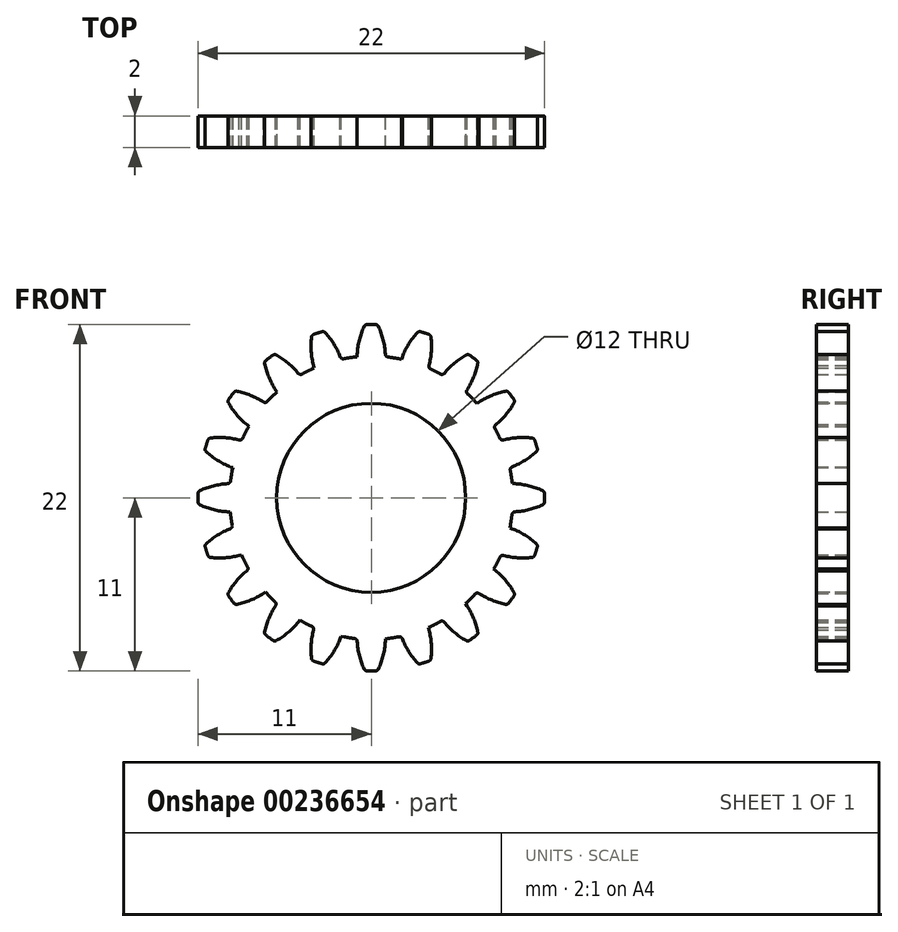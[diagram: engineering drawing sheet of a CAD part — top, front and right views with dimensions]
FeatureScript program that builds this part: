
annotation { "Feature Type Name" : "Feature", "Feature Type Description" : "" }
export const myFeature = defineFeature(function(context is Context, id is Id, definition is map)
    precondition{}
    {
        {
            var Q0;
            Q0=qCreatedBy(makeId("Front.planeOp"),FACE);
            var sketch = newSketch(context, id + "F0", { "sketchPlane" : qUnion([Q0])});
            skArc(sketch, "E0.0", {"start": v(1.74, 8.83) * mm, "mid": v(1.4, 8.89) * mm, "end": v(1.07, 8.94) * mm});
            skArc(sketch, "E1", {"start": v(0.9, 9.12) * mm, "mid": v(0.76, 10.02) * mm, "end": v(0.45, 10.88) * mm});
            skArc(sketch, "E2.MirrorCS", {"start": v(-0.9, 9.12) * mm, "mid": v(-0.76, 10.02) * mm, "end": v(-0.45, 10.88) * mm});
            skArc(sketch, "E3.trimOffspring", {"start": v(0.28, 11) * mm, "mid": v(0, 11) * mm, "end": v(-0.28, 11) * mm});
            skPoint(sketch, "E4.visualSharp", {"position": v(0.9, 8.95) * mm});
            skArc(sketch, "E4.filletArc", {"start": v(0.9, 9.12) * mm, "mid": v(0.95, 9) * mm, "end": v(1.07, 8.94) * mm});
            skPoint(sketch, "E5.visualSharp", {"position": v(-0.9, 8.95) * mm});
            skPoint(sketch, "E6.visualSharp", {"position": v(10.33, 3.78) * mm});
            skPoint(sketch, "E7.visualSharp", {"position": v(1.91, 8.8) * mm});
            skPoint(sketch, "E8.visualSharp", {"position": v(-0.4, 11) * mm});
            skArc(sketch, "E8.filletArc", {"start": v(-0.28, 11) * mm, "mid": v(-0.38, 10.96) * mm, "end": v(-0.45, 10.88) * mm});
            skPoint(sketch, "E9.visualSharp", {"position": v(0.4, 11) * mm});
            skArc(sketch, "E9.filletArc", {"start": v(0.45, 10.88) * mm, "mid": v(0.38, 10.96) * mm, "end": v(0.28, 11) * mm});
            skPoint(sketch, "E10.orphan", {"position": v(6.72, 6) * mm});
            skPoint(sketch, "E11.orphan", {"position": v(8.24, -3.62) * mm});
            skPoint(sketch, "E12.orphan", {"position": v(3.02, -10.58) * mm});
            skPoint(sketch, "E13.orphan", {"position": v(-6.78, -8.66) * mm});
            skPoint(sketch, "E14.orphan", {"position": v(-8.66, -6.78) * mm});
            skPoint(sketch, "E15.orphan", {"position": v(-9.13, -6.14) * mm});
            skPoint(sketch, "E16.orphan", {"position": v(-10.58, -3.02) * mm});
            skPoint(sketch, "E17.orphan", {"position": v(-11, 0.4) * mm});
            skPoint(sketch, "E18.orphan", {"position": v(-8.8, 1.91) * mm});
            skPoint(sketch, "E19.orphan", {"position": v(-10.33, 3.78) * mm});
            skPoint(sketch, "E20.orphan", {"position": v(-8.66, 6.78) * mm});
            skPoint(sketch, "E21.orphan", {"position": v(-4.54, 7.77) * mm});
            skLineSegment(sketch, "E22", {"start": v(0, 0) * mm, "end": v(-0.9, 8.95) * mm});
            skLineSegment(sketch, "E23", {"start": v(-0.9, 9.12) * mm, "end": v(-0.9, 8.95) * mm});
            skLineSegment(sketch, "E24", {"start": v(1.74, 8.83) * mm, "end": v(1.91, 8.8) * mm});
            skLineSegment(sketch, "E25", {"start": v(1.91, 8.8) * mm, "end": v(0, 0) * mm});
            skSolve(sketch);
        }
        {
            var Q0;
            Q0=makeQuery(id+"F0.imprint","IMPRINT",FACE,{"disambiguationData":[TD([[makeQuery(id+"F0.imprint","IMPRINT",EDGE,{"derivedFrom":sQuery(id+"F0.wireOp",EDGE,"E0.0")}),1.0]])]});
            extrude(context, id + "F1", {"entities" : qUnion([Q0]), "depth" : 2 * mm});
        }
        {
            var Q0;
            Q0=makeQuery(id+"F1.opExtrude","SWEPT_BODY",BODY,{"disambiguationData":[OSD([sQuery(id+"F0.wireOp",EDGE,"E0.0"),sQuery(id+"F0.wireOp",EDGE,"E1"),sQuery(id+"F0.wireOp",EDGE,"E2.MirrorCS"),sQuery(id+"F0.wireOp",EDGE,"E3.trimOffspring"),sQuery(id+"F0.wireOp",EDGE,"E4.filletArc"),sQuery(id+"F0.wireOp",EDGE,"E8.filletArc"),sQuery(id+"F0.wireOp",EDGE,"E9.filletArc"),sQuery(id+"F0.wireOp",EDGE,"E22"),sQuery(id+"F0.wireOp",EDGE,"E23"),sQuery(id+"F0.wireOp",EDGE,"E24"),sQuery(id+"F0.wireOp",EDGE,"E25")])]});
            var Q1;
            Q1=makeQuery(id+"F1.opExtrude","SWEPT_EDGE",EDGE,{"disambiguationData":[OSD([sQuery(id+"F0.wireOp",EDGE,"E22"),sQuery(id+"F0.wireOp",EDGE,"E25")])]});
            circularPattern(context, id + "F2", {"entities" : qUnion([Q0]), "axis" : qUnion([Q1]), "angle" : 360 * degree, "instanceCount" : 20, "equalSpace" : true});
        }
        {
            var Q0;
            Q0=makeQuery(id+"F2.opPattern","COPY",BODY,{"derivedFrom":makeQuery(id+"F1.opExtrude","SWEPT_BODY",BODY,{"disambiguationData":[OSD([sQuery(id+"F0.wireOp",EDGE,"E0.0"),sQuery(id+"F0.wireOp",EDGE,"E1"),sQuery(id+"F0.wireOp",EDGE,"E2.MirrorCS"),sQuery(id+"F0.wireOp",EDGE,"E3.trimOffspring"),sQuery(id+"F0.wireOp",EDGE,"E4.filletArc"),sQuery(id+"F0.wireOp",EDGE,"E8.filletArc"),sQuery(id+"F0.wireOp",EDGE,"E9.filletArc"),sQuery(id+"F0.wireOp",EDGE,"E22"),sQuery(id+"F0.wireOp",EDGE,"E23"),sQuery(id+"F0.wireOp",EDGE,"E24"),sQuery(id+"F0.wireOp",EDGE,"E25")])]}),"instanceName":"1"});
            var Q1;
            Q1=makeQuery(id+"F2.opPattern","COPY",BODY,{"derivedFrom":makeQuery(id+"F1.opExtrude","SWEPT_BODY",BODY,{"disambiguationData":[OSD([sQuery(id+"F0.wireOp",EDGE,"E0.0"),sQuery(id+"F0.wireOp",EDGE,"E1"),sQuery(id+"F0.wireOp",EDGE,"E2.MirrorCS"),sQuery(id+"F0.wireOp",EDGE,"E3.trimOffspring"),sQuery(id+"F0.wireOp",EDGE,"E4.filletArc"),sQuery(id+"F0.wireOp",EDGE,"E8.filletArc"),sQuery(id+"F0.wireOp",EDGE,"E9.filletArc"),sQuery(id+"F0.wireOp",EDGE,"E22"),sQuery(id+"F0.wireOp",EDGE,"E23"),sQuery(id+"F0.wireOp",EDGE,"E24"),sQuery(id+"F0.wireOp",EDGE,"E25")])]}),"instanceName":"19"});
            var Q2;
            Q2=makeQuery(id+"F2.opPattern","COPY",BODY,{"derivedFrom":makeQuery(id+"F1.opExtrude","SWEPT_BODY",BODY,{"disambiguationData":[OSD([sQuery(id+"F0.wireOp",EDGE,"E0.0"),sQuery(id+"F0.wireOp",EDGE,"E1"),sQuery(id+"F0.wireOp",EDGE,"E2.MirrorCS"),sQuery(id+"F0.wireOp",EDGE,"E3.trimOffspring"),sQuery(id+"F0.wireOp",EDGE,"E4.filletArc"),sQuery(id+"F0.wireOp",EDGE,"E8.filletArc"),sQuery(id+"F0.wireOp",EDGE,"E9.filletArc"),sQuery(id+"F0.wireOp",EDGE,"E22"),sQuery(id+"F0.wireOp",EDGE,"E23"),sQuery(id+"F0.wireOp",EDGE,"E24"),sQuery(id+"F0.wireOp",EDGE,"E25")])]}),"instanceName":"18"});
            var Q3;
            Q3=makeQuery(id+"F2.opPattern","COPY",BODY,{"derivedFrom":makeQuery(id+"F1.opExtrude","SWEPT_BODY",BODY,{"disambiguationData":[OSD([sQuery(id+"F0.wireOp",EDGE,"E0.0"),sQuery(id+"F0.wireOp",EDGE,"E1"),sQuery(id+"F0.wireOp",EDGE,"E2.MirrorCS"),sQuery(id+"F0.wireOp",EDGE,"E3.trimOffspring"),sQuery(id+"F0.wireOp",EDGE,"E4.filletArc"),sQuery(id+"F0.wireOp",EDGE,"E8.filletArc"),sQuery(id+"F0.wireOp",EDGE,"E9.filletArc"),sQuery(id+"F0.wireOp",EDGE,"E22"),sQuery(id+"F0.wireOp",EDGE,"E23"),sQuery(id+"F0.wireOp",EDGE,"E24"),sQuery(id+"F0.wireOp",EDGE,"E25")])]}),"instanceName":"17"});
            var Q4;
            Q4=makeQuery(id+"F2.opPattern","COPY",BODY,{"derivedFrom":makeQuery(id+"F1.opExtrude","SWEPT_BODY",BODY,{"disambiguationData":[OSD([sQuery(id+"F0.wireOp",EDGE,"E0.0"),sQuery(id+"F0.wireOp",EDGE,"E1"),sQuery(id+"F0.wireOp",EDGE,"E2.MirrorCS"),sQuery(id+"F0.wireOp",EDGE,"E3.trimOffspring"),sQuery(id+"F0.wireOp",EDGE,"E4.filletArc"),sQuery(id+"F0.wireOp",EDGE,"E8.filletArc"),sQuery(id+"F0.wireOp",EDGE,"E9.filletArc"),sQuery(id+"F0.wireOp",EDGE,"E22"),sQuery(id+"F0.wireOp",EDGE,"E23"),sQuery(id+"F0.wireOp",EDGE,"E24"),sQuery(id+"F0.wireOp",EDGE,"E25")])]}),"instanceName":"16"});
            var Q5;
            Q5=makeQuery(id+"F2.opPattern","COPY",BODY,{"derivedFrom":makeQuery(id+"F1.opExtrude","SWEPT_BODY",BODY,{"disambiguationData":[OSD([sQuery(id+"F0.wireOp",EDGE,"E0.0"),sQuery(id+"F0.wireOp",EDGE,"E1"),sQuery(id+"F0.wireOp",EDGE,"E2.MirrorCS"),sQuery(id+"F0.wireOp",EDGE,"E3.trimOffspring"),sQuery(id+"F0.wireOp",EDGE,"E4.filletArc"),sQuery(id+"F0.wireOp",EDGE,"E8.filletArc"),sQuery(id+"F0.wireOp",EDGE,"E9.filletArc"),sQuery(id+"F0.wireOp",EDGE,"E22"),sQuery(id+"F0.wireOp",EDGE,"E23"),sQuery(id+"F0.wireOp",EDGE,"E24"),sQuery(id+"F0.wireOp",EDGE,"E25")])]}),"instanceName":"15"});
            var Q6;
            Q6=makeQuery(id+"F2.opPattern","COPY",BODY,{"derivedFrom":makeQuery(id+"F1.opExtrude","SWEPT_BODY",BODY,{"disambiguationData":[OSD([sQuery(id+"F0.wireOp",EDGE,"E0.0"),sQuery(id+"F0.wireOp",EDGE,"E1"),sQuery(id+"F0.wireOp",EDGE,"E2.MirrorCS"),sQuery(id+"F0.wireOp",EDGE,"E3.trimOffspring"),sQuery(id+"F0.wireOp",EDGE,"E4.filletArc"),sQuery(id+"F0.wireOp",EDGE,"E8.filletArc"),sQuery(id+"F0.wireOp",EDGE,"E9.filletArc"),sQuery(id+"F0.wireOp",EDGE,"E22"),sQuery(id+"F0.wireOp",EDGE,"E23"),sQuery(id+"F0.wireOp",EDGE,"E24"),sQuery(id+"F0.wireOp",EDGE,"E25")])]}),"instanceName":"14"});
            var Q7;
            Q7=makeQuery(id+"F2.opPattern","COPY",BODY,{"derivedFrom":makeQuery(id+"F1.opExtrude","SWEPT_BODY",BODY,{"disambiguationData":[OSD([sQuery(id+"F0.wireOp",EDGE,"E0.0"),sQuery(id+"F0.wireOp",EDGE,"E1"),sQuery(id+"F0.wireOp",EDGE,"E2.MirrorCS"),sQuery(id+"F0.wireOp",EDGE,"E3.trimOffspring"),sQuery(id+"F0.wireOp",EDGE,"E4.filletArc"),sQuery(id+"F0.wireOp",EDGE,"E8.filletArc"),sQuery(id+"F0.wireOp",EDGE,"E9.filletArc"),sQuery(id+"F0.wireOp",EDGE,"E22"),sQuery(id+"F0.wireOp",EDGE,"E23"),sQuery(id+"F0.wireOp",EDGE,"E24"),sQuery(id+"F0.wireOp",EDGE,"E25")])]}),"instanceName":"13"});
            var Q8;
            Q8=makeQuery(id+"F2.opPattern","COPY",BODY,{"derivedFrom":makeQuery(id+"F1.opExtrude","SWEPT_BODY",BODY,{"disambiguationData":[OSD([sQuery(id+"F0.wireOp",EDGE,"E0.0"),sQuery(id+"F0.wireOp",EDGE,"E1"),sQuery(id+"F0.wireOp",EDGE,"E2.MirrorCS"),sQuery(id+"F0.wireOp",EDGE,"E3.trimOffspring"),sQuery(id+"F0.wireOp",EDGE,"E4.filletArc"),sQuery(id+"F0.wireOp",EDGE,"E8.filletArc"),sQuery(id+"F0.wireOp",EDGE,"E9.filletArc"),sQuery(id+"F0.wireOp",EDGE,"E22"),sQuery(id+"F0.wireOp",EDGE,"E23"),sQuery(id+"F0.wireOp",EDGE,"E24"),sQuery(id+"F0.wireOp",EDGE,"E25")])]}),"instanceName":"12"});
            var Q9;
            Q9=makeQuery(id+"F2.opPattern","COPY",BODY,{"derivedFrom":makeQuery(id+"F1.opExtrude","SWEPT_BODY",BODY,{"disambiguationData":[OSD([sQuery(id+"F0.wireOp",EDGE,"E0.0"),sQuery(id+"F0.wireOp",EDGE,"E1"),sQuery(id+"F0.wireOp",EDGE,"E2.MirrorCS"),sQuery(id+"F0.wireOp",EDGE,"E3.trimOffspring"),sQuery(id+"F0.wireOp",EDGE,"E4.filletArc"),sQuery(id+"F0.wireOp",EDGE,"E8.filletArc"),sQuery(id+"F0.wireOp",EDGE,"E9.filletArc"),sQuery(id+"F0.wireOp",EDGE,"E22"),sQuery(id+"F0.wireOp",EDGE,"E23"),sQuery(id+"F0.wireOp",EDGE,"E24"),sQuery(id+"F0.wireOp",EDGE,"E25")])]}),"instanceName":"11"});
            var Q10;
            Q10=makeQuery(id+"F2.opPattern","COPY",BODY,{"derivedFrom":makeQuery(id+"F1.opExtrude","SWEPT_BODY",BODY,{"disambiguationData":[OSD([sQuery(id+"F0.wireOp",EDGE,"E0.0"),sQuery(id+"F0.wireOp",EDGE,"E1"),sQuery(id+"F0.wireOp",EDGE,"E2.MirrorCS"),sQuery(id+"F0.wireOp",EDGE,"E3.trimOffspring"),sQuery(id+"F0.wireOp",EDGE,"E4.filletArc"),sQuery(id+"F0.wireOp",EDGE,"E8.filletArc"),sQuery(id+"F0.wireOp",EDGE,"E9.filletArc"),sQuery(id+"F0.wireOp",EDGE,"E22"),sQuery(id+"F0.wireOp",EDGE,"E23"),sQuery(id+"F0.wireOp",EDGE,"E24"),sQuery(id+"F0.wireOp",EDGE,"E25")])]}),"instanceName":"10"});
            var Q11;
            Q11=makeQuery(id+"F2.opPattern","COPY",BODY,{"derivedFrom":makeQuery(id+"F1.opExtrude","SWEPT_BODY",BODY,{"disambiguationData":[OSD([sQuery(id+"F0.wireOp",EDGE,"E0.0"),sQuery(id+"F0.wireOp",EDGE,"E1"),sQuery(id+"F0.wireOp",EDGE,"E2.MirrorCS"),sQuery(id+"F0.wireOp",EDGE,"E3.trimOffspring"),sQuery(id+"F0.wireOp",EDGE,"E4.filletArc"),sQuery(id+"F0.wireOp",EDGE,"E8.filletArc"),sQuery(id+"F0.wireOp",EDGE,"E9.filletArc"),sQuery(id+"F0.wireOp",EDGE,"E22"),sQuery(id+"F0.wireOp",EDGE,"E23"),sQuery(id+"F0.wireOp",EDGE,"E24"),sQuery(id+"F0.wireOp",EDGE,"E25")])]}),"instanceName":"9"});
            var Q12;
            Q12=makeQuery(id+"F2.opPattern","COPY",BODY,{"derivedFrom":makeQuery(id+"F1.opExtrude","SWEPT_BODY",BODY,{"disambiguationData":[OSD([sQuery(id+"F0.wireOp",EDGE,"E0.0"),sQuery(id+"F0.wireOp",EDGE,"E1"),sQuery(id+"F0.wireOp",EDGE,"E2.MirrorCS"),sQuery(id+"F0.wireOp",EDGE,"E3.trimOffspring"),sQuery(id+"F0.wireOp",EDGE,"E4.filletArc"),sQuery(id+"F0.wireOp",EDGE,"E8.filletArc"),sQuery(id+"F0.wireOp",EDGE,"E9.filletArc"),sQuery(id+"F0.wireOp",EDGE,"E22"),sQuery(id+"F0.wireOp",EDGE,"E23"),sQuery(id+"F0.wireOp",EDGE,"E24"),sQuery(id+"F0.wireOp",EDGE,"E25")])]}),"instanceName":"8"});
            var Q13;
            Q13=makeQuery(id+"F2.opPattern","COPY",BODY,{"derivedFrom":makeQuery(id+"F1.opExtrude","SWEPT_BODY",BODY,{"disambiguationData":[OSD([sQuery(id+"F0.wireOp",EDGE,"E0.0"),sQuery(id+"F0.wireOp",EDGE,"E1"),sQuery(id+"F0.wireOp",EDGE,"E2.MirrorCS"),sQuery(id+"F0.wireOp",EDGE,"E3.trimOffspring"),sQuery(id+"F0.wireOp",EDGE,"E4.filletArc"),sQuery(id+"F0.wireOp",EDGE,"E8.filletArc"),sQuery(id+"F0.wireOp",EDGE,"E9.filletArc"),sQuery(id+"F0.wireOp",EDGE,"E22"),sQuery(id+"F0.wireOp",EDGE,"E23"),sQuery(id+"F0.wireOp",EDGE,"E24"),sQuery(id+"F0.wireOp",EDGE,"E25")])]}),"instanceName":"7"});
            var Q14;
            Q14=makeQuery(id+"F2.opPattern","COPY",BODY,{"derivedFrom":makeQuery(id+"F1.opExtrude","SWEPT_BODY",BODY,{"disambiguationData":[OSD([sQuery(id+"F0.wireOp",EDGE,"E0.0"),sQuery(id+"F0.wireOp",EDGE,"E1"),sQuery(id+"F0.wireOp",EDGE,"E2.MirrorCS"),sQuery(id+"F0.wireOp",EDGE,"E3.trimOffspring"),sQuery(id+"F0.wireOp",EDGE,"E4.filletArc"),sQuery(id+"F0.wireOp",EDGE,"E8.filletArc"),sQuery(id+"F0.wireOp",EDGE,"E9.filletArc"),sQuery(id+"F0.wireOp",EDGE,"E22"),sQuery(id+"F0.wireOp",EDGE,"E23"),sQuery(id+"F0.wireOp",EDGE,"E24"),sQuery(id+"F0.wireOp",EDGE,"E25")])]}),"instanceName":"6"});
            var Q15;
            Q15=makeQuery(id+"F2.opPattern","COPY",BODY,{"derivedFrom":makeQuery(id+"F1.opExtrude","SWEPT_BODY",BODY,{"disambiguationData":[OSD([sQuery(id+"F0.wireOp",EDGE,"E0.0"),sQuery(id+"F0.wireOp",EDGE,"E1"),sQuery(id+"F0.wireOp",EDGE,"E2.MirrorCS"),sQuery(id+"F0.wireOp",EDGE,"E3.trimOffspring"),sQuery(id+"F0.wireOp",EDGE,"E4.filletArc"),sQuery(id+"F0.wireOp",EDGE,"E8.filletArc"),sQuery(id+"F0.wireOp",EDGE,"E9.filletArc"),sQuery(id+"F0.wireOp",EDGE,"E22"),sQuery(id+"F0.wireOp",EDGE,"E23"),sQuery(id+"F0.wireOp",EDGE,"E24"),sQuery(id+"F0.wireOp",EDGE,"E25")])]}),"instanceName":"5"});
            var Q16;
            Q16=makeQuery(id+"F2.opPattern","COPY",BODY,{"derivedFrom":makeQuery(id+"F1.opExtrude","SWEPT_BODY",BODY,{"disambiguationData":[OSD([sQuery(id+"F0.wireOp",EDGE,"E0.0"),sQuery(id+"F0.wireOp",EDGE,"E1"),sQuery(id+"F0.wireOp",EDGE,"E2.MirrorCS"),sQuery(id+"F0.wireOp",EDGE,"E3.trimOffspring"),sQuery(id+"F0.wireOp",EDGE,"E4.filletArc"),sQuery(id+"F0.wireOp",EDGE,"E8.filletArc"),sQuery(id+"F0.wireOp",EDGE,"E9.filletArc"),sQuery(id+"F0.wireOp",EDGE,"E22"),sQuery(id+"F0.wireOp",EDGE,"E23"),sQuery(id+"F0.wireOp",EDGE,"E24"),sQuery(id+"F0.wireOp",EDGE,"E25")])]}),"instanceName":"4"});
            var Q17;
            Q17=makeQuery(id+"F2.opPattern","COPY",BODY,{"derivedFrom":makeQuery(id+"F1.opExtrude","SWEPT_BODY",BODY,{"disambiguationData":[OSD([sQuery(id+"F0.wireOp",EDGE,"E0.0"),sQuery(id+"F0.wireOp",EDGE,"E1"),sQuery(id+"F0.wireOp",EDGE,"E2.MirrorCS"),sQuery(id+"F0.wireOp",EDGE,"E3.trimOffspring"),sQuery(id+"F0.wireOp",EDGE,"E4.filletArc"),sQuery(id+"F0.wireOp",EDGE,"E8.filletArc"),sQuery(id+"F0.wireOp",EDGE,"E9.filletArc"),sQuery(id+"F0.wireOp",EDGE,"E22"),sQuery(id+"F0.wireOp",EDGE,"E23"),sQuery(id+"F0.wireOp",EDGE,"E24"),sQuery(id+"F0.wireOp",EDGE,"E25")])]}),"instanceName":"3"});
            var Q18;
            Q18=makeQuery(id+"F2.opPattern","COPY",BODY,{"derivedFrom":makeQuery(id+"F1.opExtrude","SWEPT_BODY",BODY,{"disambiguationData":[OSD([sQuery(id+"F0.wireOp",EDGE,"E0.0"),sQuery(id+"F0.wireOp",EDGE,"E1"),sQuery(id+"F0.wireOp",EDGE,"E2.MirrorCS"),sQuery(id+"F0.wireOp",EDGE,"E3.trimOffspring"),sQuery(id+"F0.wireOp",EDGE,"E4.filletArc"),sQuery(id+"F0.wireOp",EDGE,"E8.filletArc"),sQuery(id+"F0.wireOp",EDGE,"E9.filletArc"),sQuery(id+"F0.wireOp",EDGE,"E22"),sQuery(id+"F0.wireOp",EDGE,"E23"),sQuery(id+"F0.wireOp",EDGE,"E24"),sQuery(id+"F0.wireOp",EDGE,"E25")])]}),"instanceName":"2"});
            var Q19;
            Q19=makeQuery(id+"F1.opExtrude","SWEPT_BODY",BODY,{"disambiguationData":[OSD([sQuery(id+"F0.wireOp",EDGE,"E0.0"),sQuery(id+"F0.wireOp",EDGE,"E1"),sQuery(id+"F0.wireOp",EDGE,"E2.MirrorCS"),sQuery(id+"F0.wireOp",EDGE,"E3.trimOffspring"),sQuery(id+"F0.wireOp",EDGE,"E4.filletArc"),sQuery(id+"F0.wireOp",EDGE,"E8.filletArc"),sQuery(id+"F0.wireOp",EDGE,"E9.filletArc"),sQuery(id+"F0.wireOp",EDGE,"E22"),sQuery(id+"F0.wireOp",EDGE,"E23"),sQuery(id+"F0.wireOp",EDGE,"E24"),sQuery(id+"F0.wireOp",EDGE,"E25")])]});
            booleanBodies(context, id + "F3", {"operationType" : BooleanOperationType.UNION, "tools" : qUnion([Q0, Q1, Q2, Q3, Q4, Q5, Q6, Q7, Q8, Q9, Q10, Q11, Q12, Q13, Q14, Q15, Q16, Q17, Q18, Q19])});
        }
        {
            var Q0;
            Q0=makeQuery(id+"F3.opBoolean","MERGE",EDGE,{"derivedFrom":[makeQuery(id+"F2.opPattern","COPY",EDGE,{"derivedFrom":makeQuery(id+"F1.opExtrude","SWEPT_EDGE",EDGE,{"disambiguationData":[OSD([sQuery(id+"F0.wireOp",EDGE,"E24"),sQuery(id+"F0.wireOp",EDGE,"E25")])]}),"instanceName":"3"}),makeQuery(id+"F2.opPattern","COPY",EDGE,{"derivedFrom":makeQuery(id+"F1.opExtrude","SWEPT_EDGE",EDGE,{"disambiguationData":[OSD([sQuery(id+"F0.wireOp",EDGE,"E22"),sQuery(id+"F0.wireOp",EDGE,"E23")])]}),"instanceName":"4"})]});
            fillet(context, id + "F4", {"entities" : qUnion([Q0]), "radius" : 0.2 * mm, "tangentPropagation" : true, "allowEdgeOverflow" : false});
        }
        {
            var Q0;
            Q0=makeQuery(id+"F3.opBoolean","MERGE",EDGE,{"derivedFrom":[makeQuery(id+"F2.opPattern","COPY",EDGE,{"derivedFrom":makeQuery(id+"F1.opExtrude","SWEPT_EDGE",EDGE,{"disambiguationData":[OSD([sQuery(id+"F0.wireOp",EDGE,"E24"),sQuery(id+"F0.wireOp",EDGE,"E25")])]}),"instanceName":"1"}),makeQuery(id+"F2.opPattern","COPY",EDGE,{"derivedFrom":makeQuery(id+"F1.opExtrude","SWEPT_EDGE",EDGE,{"disambiguationData":[OSD([sQuery(id+"F0.wireOp",EDGE,"E22"),sQuery(id+"F0.wireOp",EDGE,"E23")])]}),"instanceName":"2"})]});
            fillet(context, id + "F5", {"entities" : qUnion([Q0]), "radius" : 0.2 * mm, "tangentPropagation" : true, "allowEdgeOverflow" : false});
        }
        {
            var Q0;
            {var subQ0=makeQuery(id+"F1.opExtrude","CAP_FACE",FACE,{"disambiguationData":[OSD([sQuery(id+"F0.wireOp",EDGE,"E0.0"),sQuery(id+"F0.wireOp",EDGE,"E1"),sQuery(id+"F0.wireOp",EDGE,"E2.MirrorCS"),sQuery(id+"F0.wireOp",EDGE,"E3.trimOffspring"),sQuery(id+"F0.wireOp",EDGE,"E4.filletArc"),sQuery(id+"F0.wireOp",EDGE,"E8.filletArc"),sQuery(id+"F0.wireOp",EDGE,"E9.filletArc"),sQuery(id+"F0.wireOp",EDGE,"E22"),sQuery(id+"F0.wireOp",EDGE,"E23"),sQuery(id+"F0.wireOp",EDGE,"E24"),sQuery(id+"F0.wireOp",EDGE,"E25")])],"isStart":false});Q0=makeQuery(id+"F3.opBoolean","MERGE",FACE,{"derivedFrom":[subQ0,makeQuery(id+"F2.opPattern","COPY",FACE,{"derivedFrom":subQ0,"instanceName":"1"}),makeQuery(id+"F2.opPattern","COPY",FACE,{"derivedFrom":subQ0,"instanceName":"2"}),makeQuery(id+"F2.opPattern","COPY",FACE,{"derivedFrom":subQ0,"instanceName":"3"}),makeQuery(id+"F2.opPattern","COPY",FACE,{"derivedFrom":subQ0,"instanceName":"4"}),makeQuery(id+"F2.opPattern","COPY",FACE,{"derivedFrom":subQ0,"instanceName":"5"}),makeQuery(id+"F2.opPattern","COPY",FACE,{"derivedFrom":subQ0,"instanceName":"6"}),makeQuery(id+"F2.opPattern","COPY",FACE,{"derivedFrom":subQ0,"instanceName":"7"}),makeQuery(id+"F2.opPattern","COPY",FACE,{"derivedFrom":subQ0,"instanceName":"8"}),makeQuery(id+"F2.opPattern","COPY",FACE,{"derivedFrom":subQ0,"instanceName":"9"}),makeQuery(id+"F2.opPattern","COPY",FACE,{"derivedFrom":subQ0,"instanceName":"10"}),makeQuery(id+"F2.opPattern","COPY",FACE,{"derivedFrom":subQ0,"instanceName":"11"}),makeQuery(id+"F2.opPattern","COPY",FACE,{"derivedFrom":subQ0,"instanceName":"12"}),makeQuery(id+"F2.opPattern","COPY",FACE,{"derivedFrom":subQ0,"instanceName":"13"}),makeQuery(id+"F2.opPattern","COPY",FACE,{"derivedFrom":subQ0,"instanceName":"14"}),makeQuery(id+"F2.opPattern","COPY",FACE,{"derivedFrom":subQ0,"instanceName":"15"}),makeQuery(id+"F2.opPattern","COPY",FACE,{"derivedFrom":subQ0,"instanceName":"16"}),makeQuery(id+"F2.opPattern","COPY",FACE,{"derivedFrom":subQ0,"instanceName":"17"}),makeQuery(id+"F2.opPattern","COPY",FACE,{"derivedFrom":subQ0,"instanceName":"18"}),makeQuery(id+"F2.opPattern","COPY",FACE,{"derivedFrom":subQ0,"instanceName":"19"})]});}
            var sketch = newSketch(context, id + "F6", { "sketchPlane" : qUnion([Q0])});
            skPoint(sketch, "E26", {"position": v(0, 0) * mm});
            skSolve(sketch);
        }
        {
            var Q0;
            Q0=sQuery(id+"F6.wireOp",VERTEX,"E26");
            var Q1;
            Q1=makeQuery(id+"F2.opPattern","COPY",BODY,{"derivedFrom":makeQuery(id+"F1.opExtrude","SWEPT_BODY",BODY,{"disambiguationData":[OSD([sQuery(id+"F0.wireOp",EDGE,"E0.0"),sQuery(id+"F0.wireOp",EDGE,"E1"),sQuery(id+"F0.wireOp",EDGE,"E2.MirrorCS"),sQuery(id+"F0.wireOp",EDGE,"E3.trimOffspring"),sQuery(id+"F0.wireOp",EDGE,"E4.filletArc"),sQuery(id+"F0.wireOp",EDGE,"E8.filletArc"),sQuery(id+"F0.wireOp",EDGE,"E9.filletArc"),sQuery(id+"F0.wireOp",EDGE,"E22"),sQuery(id+"F0.wireOp",EDGE,"E23"),sQuery(id+"F0.wireOp",EDGE,"E24"),sQuery(id+"F0.wireOp",EDGE,"E25")])]}),"instanceName":"1"});
            hole(context, id + "F7", {"style" : HoleStyle.SIMPLE, "endStyle" : HoleEndStyle.THROUGH, "holeDiameter" : 12 * mm, "locations" : qUnion([Q0]), "scope" : qUnion([Q1]), "isTappedThrough" : true});
        }
    });
